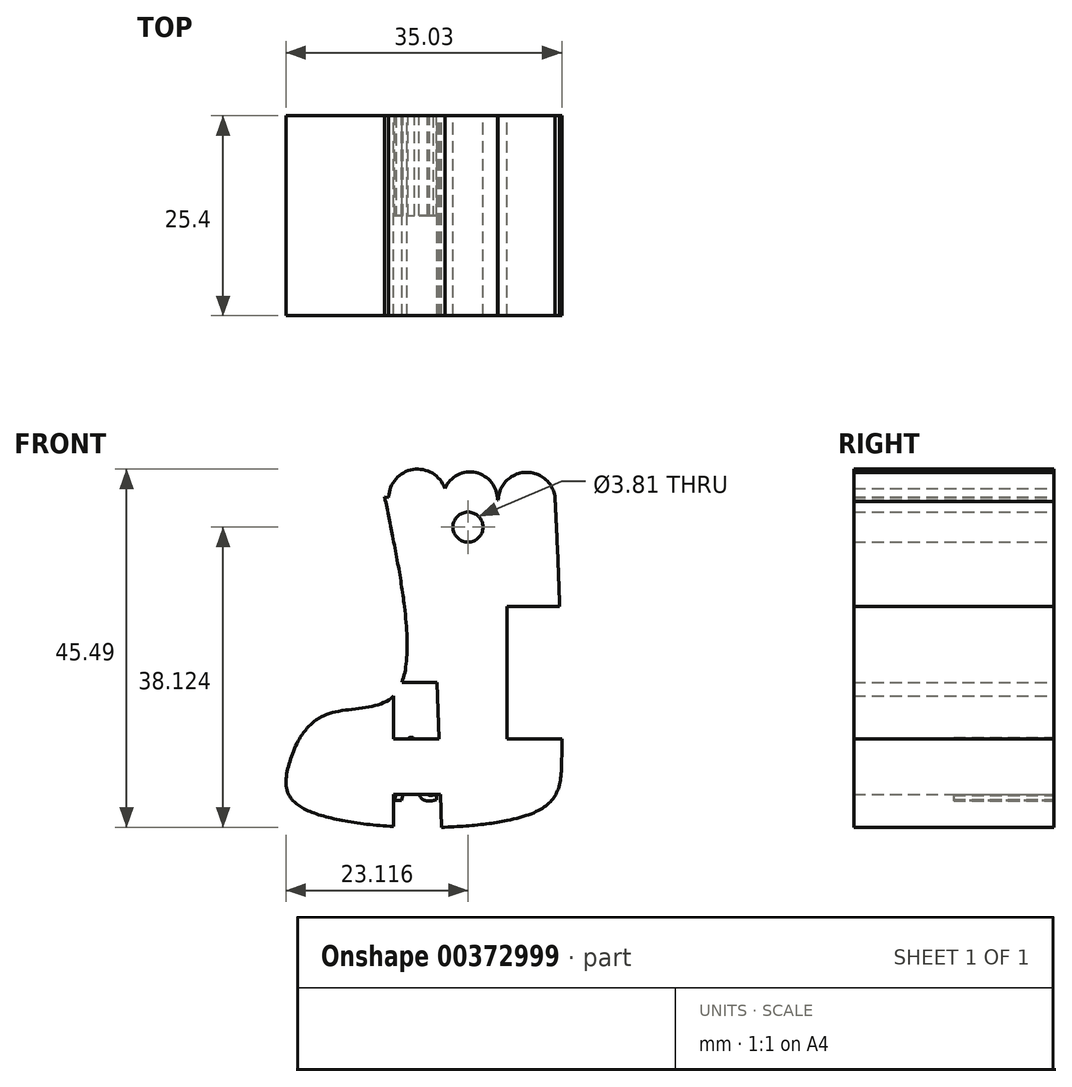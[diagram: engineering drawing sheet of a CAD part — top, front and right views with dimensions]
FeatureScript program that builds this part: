
annotation { "Feature Type Name" : "Feature", "Feature Type Description" : "" }
export const myFeature = defineFeature(function(context is Context, id is Id, definition is map)
    precondition{}
    {
        {
            var Q0;
            Q0=qCreatedBy(makeId("Front.planeOp"),FACE);
            var sketch = newSketch(context, id + "F0", { "sketchPlane" : qUnion([Q0])});
            skLineSegment(sketch, "E0", {"start": v(-9.1, 9.51) * mm, "end": v(-9.1, 12.05) * mm});
            skLineSegment(sketch, "E1", {"start": v(-34.55, 9.51) * mm, "end": v(-34.55, 12.05) * mm});
            skPoint(sketch, "E2.orphan", {"position": v(-34.55, 34.91) * mm});
            skPoint(sketch, "E3.orphan", {"position": v(-9.1, 34.91) * mm});
            skFitSpline(sketch, "E4", {"points": [v(16.98, 45.2) * mm, v(18.1, 19.94) * mm, v(9.2, 17.45) * mm, v(4.77, 11.06) * mm, v(6.43, 5.79) * mm, v(36.14, 5.23) * mm, v(39.47, 12.45) * mm, v(39.2, 31.33) * mm, v(38.64, 44.65) * mm], "startDerivative": vector(39.66, -192.65) * mm, "endDerivative": vector(-4.86, 99.16) * mm});
            skLineSegment(sketch, "E5", {"start": v(16.98, 45.2) * mm, "end": v(38.64, 44.65) * mm});
            skArc(sketch, "E6", {"start": v(24.55, 43.7) * mm, "mid": v(21.91, 48.69) * mm, "end": v(17.5, 45.2) * mm});
            skArc(sketch, "E7", {"start": v(31.29, 44.84) * mm, "mid": v(27.23, 48.36) * mm, "end": v(24.55, 43.7) * mm});
            skArc(sketch, "E8", {"start": v(38.64, 44.65) * mm, "mid": v(35.1, 48.37) * mm, "end": v(31.4, 44.84) * mm});
            skLineSegment(sketch, "E9", {"start": v(18.05, 39.93) * mm, "end": v(38.84, 40.56) * mm});
            skLineSegment(sketch, "E10", {"start": v(9.2, 17.45) * mm, "end": v(9.2, 4.69) * mm});
            skLineSegment(sketch, "E11", {"start": v(18.1, 19.94) * mm, "end": v(18.1, 3.37) * mm});
            skLineSegment(sketch, "E12", {"start": v(23.08, 40.08) * mm, "end": v(24.2, 3.28) * mm});
            skLineSegment(sketch, "E13", {"start": v(32.51, 40.36) * mm, "end": v(32.51, 4.13) * mm});
            skLineSegment(sketch, "E14", {"start": v(19.24, 31.33) * mm, "end": v(39.2, 31.33) * mm});
            skLineSegment(sketch, "E15", {"start": v(18.1, 21.68) * mm, "end": v(39.4, 21.68) * mm});
            skPoint(sketch, "E15.startSnap0", {"position": v(23.64, 21.68) * mm});
            skPoint(sketch, "E15.endSnap0", {"position": v(23.64, 21.68) * mm});
            skLineSegment(sketch, "E16", {"start": v(6.16, 14.53) * mm, "end": v(39.47, 14.53) * mm});
            skLineSegment(sketch, "E17", {"start": v(4.77, 7.46) * mm, "end": v(38.71, 7.46) * mm});
            skSolve(sketch);
        }
        {
            var Q0;
            {var subQ0=sQuery(id+"F0.wireOp",EDGE,"E14");var subQ1=sQuery(id+"F0.wireOp",EDGE,"E12");var subQ2=makeQuery(id+"F0.imprint","INTERSECT",VERTEX,{"derivedFrom":[subQ1,subQ0]});Q0=makeQuery(id+"F0.imprint","IMPRINT",FACE,{"disambiguationData":[TD([[makeQuery(id+"F0.imprint","IMPRINT",EDGE,{"disambiguationData":[TD([[subQ2,-1.0]])],"derivedFrom":subQ1}),1.0]])]});}
            var Q1;
            {var subQ0=sQuery(id+"F0.wireOp",EDGE,"E12");var subQ1=sQuery(id+"F0.wireOp",EDGE,"E9");var subQ2=makeQuery(id+"F0.imprint","INTERSECT",VERTEX,{"derivedFrom":[subQ1,subQ0]});Q1=makeQuery(id+"F0.imprint","IMPRINT",FACE,{"disambiguationData":[TD([[makeQuery(id+"F0.imprint","IMPRINT",EDGE,{"disambiguationData":[TD([[subQ2,-1.0]])],"derivedFrom":subQ1}),-1.0]])]});}
            var Q2;
            {var subQ1=sQuery(id+"F0.wireOp",EDGE,"E4");var subQ7=sQuery(id+"F0.wireOp",EDGE,"E5");var subQ9=makeQuery(id+"F0.imprint","INTERSECT",VERTEX,{"derivedFrom":[subQ1,subQ7]});Q2=makeQuery(id+"F0.imprint","IMPRINT",FACE,{"disambiguationData":[TD([[makeQuery(id+"F0.imprint","IMPRINT",EDGE,{"disambiguationData":[TD([[subQ9,-1.0]])],"derivedFrom":subQ1}),1.0]])]});}
            var Q3;
            {var subQ0=sQuery(id+"F0.wireOp",EDGE,"E14");var subQ1=sQuery(id+"F0.wireOp",EDGE,"E4");var subQ2=makeQuery(id+"F0.imprint","INTERSECT",VERTEX,{"disambiguationData":[OD(0.0)],"derivedFrom":[subQ1,subQ0]});Q3=makeQuery(id+"F0.imprint","IMPRINT",FACE,{"disambiguationData":[TD([[makeQuery(id+"F0.imprint","IMPRINT",EDGE,{"disambiguationData":[TD([[subQ2,-1.0]])],"derivedFrom":subQ1}),1.0]])]});}
            var Q4;
            {var subQ0=sQuery(id+"F0.wireOp",EDGE,"E14");var subQ1=sQuery(id+"F0.wireOp",EDGE,"E4");var subQ2=makeQuery(id+"F0.imprint","INTERSECT",VERTEX,{"disambiguationData":[OD(0.0)],"derivedFrom":[subQ1,subQ0]});Q4=makeQuery(id+"F0.imprint","IMPRINT",FACE,{"disambiguationData":[TD([[makeQuery(id+"F0.imprint","IMPRINT",EDGE,{"disambiguationData":[TD([[subQ2,1.0]])],"derivedFrom":subQ1}),1.0]])]});}
            var Q5;
            {var subQ0=sQuery(id+"F0.wireOp",EDGE,"E15");var subQ1=sQuery(id+"F0.wireOp",EDGE,"E4");var subQ2=makeQuery(id+"F0.imprint","INTERSECT",VERTEX,{"disambiguationData":[OD(0.0)],"derivedFrom":[subQ1,subQ0]});Q5=makeQuery(id+"F0.imprint","IMPRINT",FACE,{"disambiguationData":[TD([[makeQuery(id+"F0.imprint","IMPRINT",EDGE,{"disambiguationData":[TD([[subQ2,1.0]])],"derivedFrom":subQ1}),1.0]])]});}
            var Q6;
            {var subQ0=sQuery(id+"F0.wireOp",EDGE,"E16");var subQ1=sQuery(id+"F0.wireOp",EDGE,"E4");var subQ2=makeQuery(id+"F0.imprint","INTERSECT",VERTEX,{"disambiguationData":[OD(1.0)],"derivedFrom":[subQ1,subQ0]});Q6=makeQuery(id+"F0.imprint","IMPRINT",FACE,{"disambiguationData":[TD([[makeQuery(id+"F0.imprint","IMPRINT",EDGE,{"disambiguationData":[TD([[subQ2,1.0]])],"derivedFrom":subQ1}),1.0]])]});}
            var Q7;
            {var subQ0=sQuery(id+"F0.wireOp",EDGE,"E12");var subQ1=sQuery(id+"F0.wireOp",EDGE,"E4");var subQ2=makeQuery(id+"F0.imprint","INTERSECT",VERTEX,{"derivedFrom":[subQ1,subQ0]});Q7=makeQuery(id+"F0.imprint","IMPRINT",FACE,{"disambiguationData":[TD([[makeQuery(id+"F0.imprint","IMPRINT",EDGE,{"disambiguationData":[TD([[subQ2,-1.0]])],"derivedFrom":subQ1}),1.0]])]});}
            var Q8;
            {var subQ0=sQuery(id+"F0.wireOp",EDGE,"E13");var subQ1=sQuery(id+"F0.wireOp",EDGE,"E4");var subQ2=makeQuery(id+"F0.imprint","INTERSECT",VERTEX,{"derivedFrom":[subQ1,subQ0]});Q8=makeQuery(id+"F0.imprint","IMPRINT",FACE,{"disambiguationData":[TD([[makeQuery(id+"F0.imprint","IMPRINT",EDGE,{"disambiguationData":[TD([[subQ2,-1.0]])],"derivedFrom":subQ1}),1.0]])]});}
            var Q9;
            {var subQ0=sQuery(id+"F0.wireOp",EDGE,"E15");var subQ1=sQuery(id+"F0.wireOp",EDGE,"E12");var subQ2=makeQuery(id+"F0.imprint","INTERSECT",VERTEX,{"derivedFrom":[subQ1,subQ0]});Q9=makeQuery(id+"F0.imprint","IMPRINT",FACE,{"disambiguationData":[TD([[makeQuery(id+"F0.imprint","IMPRINT",EDGE,{"disambiguationData":[TD([[subQ2,-1.0]])],"derivedFrom":subQ1}),1.0]])]});}
            var Q10;
            {var subQ0=sQuery(id+"F0.wireOp",EDGE,"E16");var subQ1=sQuery(id+"F0.wireOp",EDGE,"E11");var subQ2=makeQuery(id+"F0.imprint","INTERSECT",VERTEX,{"derivedFrom":[subQ1,subQ0]});Q10=makeQuery(id+"F0.imprint","IMPRINT",FACE,{"disambiguationData":[TD([[makeQuery(id+"F0.imprint","IMPRINT",EDGE,{"disambiguationData":[TD([[subQ2,-1.0]])],"derivedFrom":subQ1}),1.0]])]});}
            var Q11;
            {var subQ0=sQuery(id+"F0.wireOp",EDGE,"E9");var subQ1=sQuery(id+"F0.wireOp",EDGE,"E4");var subQ2=makeQuery(id+"F0.imprint","INTERSECT",VERTEX,{"disambiguationData":[OD(0.0)],"derivedFrom":[subQ1,subQ0]});Q11=makeQuery(id+"F0.imprint","IMPRINT",FACE,{"disambiguationData":[TD([[makeQuery(id+"F0.imprint","IMPRINT",EDGE,{"disambiguationData":[TD([[subQ2,-1.0]])],"derivedFrom":subQ1}),1.0]])]});}
            var Q12;
            {var subQ0=sQuery(id+"F0.wireOp",EDGE,"E14");var subQ1=sQuery(id+"F0.wireOp",EDGE,"E4");var subQ2=makeQuery(id+"F0.imprint","INTERSECT",VERTEX,{"disambiguationData":[OD(1.0)],"derivedFrom":[subQ1,subQ0]});Q12=makeQuery(id+"F0.imprint","IMPRINT",FACE,{"disambiguationData":[TD([[makeQuery(id+"F0.imprint","IMPRINT",EDGE,{"disambiguationData":[TD([[subQ2,-1.0]])],"derivedFrom":subQ1}),1.0]])]});}
            var Q13;
            {var subQ0=sQuery(id+"F0.wireOp",EDGE,"E10");var subQ1=sQuery(id+"F0.wireOp",EDGE,"E4");var subQ2=makeQuery(id+"F0.imprint","INTERSECT",VERTEX,{"disambiguationData":[OD(0.0)],"derivedFrom":[subQ1,subQ0]});Q13=makeQuery(id+"F0.imprint","IMPRINT",FACE,{"disambiguationData":[TD([[makeQuery(id+"F0.imprint","IMPRINT",EDGE,{"disambiguationData":[TD([[subQ2,1.0]])],"derivedFrom":subQ1}),1.0]])]});}
            var Q14;
            {var subQ0=sQuery(id+"F0.wireOp",EDGE,"E10");var subQ1=sQuery(id+"F0.wireOp",EDGE,"E4");var subQ2=makeQuery(id+"F0.imprint","INTERSECT",VERTEX,{"disambiguationData":[OD(1.0)],"derivedFrom":[subQ1,subQ0]});Q14=makeQuery(id+"F0.imprint","IMPRINT",FACE,{"disambiguationData":[TD([[makeQuery(id+"F0.imprint","IMPRINT",EDGE,{"disambiguationData":[TD([[subQ2,-1.0]])],"derivedFrom":subQ1}),1.0]])]});}
            var Q15;
            {var subQ0=sQuery(id+"F0.wireOp",EDGE,"E16");var subQ1=sQuery(id+"F0.wireOp",EDGE,"E10");var subQ2=makeQuery(id+"F0.imprint","INTERSECT",VERTEX,{"derivedFrom":[subQ1,subQ0]});Q15=makeQuery(id+"F0.imprint","IMPRINT",FACE,{"disambiguationData":[TD([[makeQuery(id+"F0.imprint","IMPRINT",EDGE,{"disambiguationData":[TD([[subQ2,-1.0]])],"derivedFrom":subQ1}),1.0]])]});}
            var Q16;
            {var subQ0=sQuery(id+"F0.wireOp",EDGE,"E11");var subQ1=sQuery(id+"F0.wireOp",EDGE,"E4");var subQ2=makeQuery(id+"F0.imprint","INTERSECT",VERTEX,{"disambiguationData":[OD(1.0)],"derivedFrom":[subQ1,subQ0]});Q16=makeQuery(id+"F0.imprint","IMPRINT",FACE,{"disambiguationData":[TD([[makeQuery(id+"F0.imprint","IMPRINT",EDGE,{"disambiguationData":[TD([[subQ2,-1.0]])],"derivedFrom":subQ1}),1.0]])]});}
            var Q17;
            {var subQ1=sQuery(id+"F0.wireOp",EDGE,"E4");var subQ7=sQuery(id+"F0.wireOp",EDGE,"E11");var subQ8=makeQuery(id+"F0.imprint","INTERSECT",VERTEX,{"disambiguationData":[OD(0.0)],"derivedFrom":[subQ1,subQ7]});Q17=makeQuery(id+"F0.imprint","IMPRINT",FACE,{"disambiguationData":[TD([[makeQuery(id+"F0.imprint","IMPRINT",EDGE,{"disambiguationData":[TD([[subQ8,1.0]])],"derivedFrom":subQ1}),1.0]])]});}
            var Q18;
            {var subQ0=sQuery(id+"F0.wireOp",EDGE,"E16");var subQ1=sQuery(id+"F0.wireOp",EDGE,"E12");var subQ2=makeQuery(id+"F0.imprint","INTERSECT",VERTEX,{"derivedFrom":[subQ1,subQ0]});Q18=makeQuery(id+"F0.imprint","IMPRINT",FACE,{"disambiguationData":[TD([[makeQuery(id+"F0.imprint","IMPRINT",EDGE,{"disambiguationData":[TD([[subQ2,-1.0]])],"derivedFrom":subQ1}),1.0]])]});}
            var Q19;
            {var subQ0=sQuery(id+"F0.wireOp",EDGE,"E6");var subQ1=sQuery(id+"F0.wireOp",EDGE,"E5");var subQ2=makeQuery(id+"F0.imprint","INTERSECT",VERTEX,{"disambiguationData":[OD(0.0)],"derivedFrom":[subQ1,subQ0]});Q19=makeQuery(id+"F0.imprint","IMPRINT",FACE,{"disambiguationData":[TD([[makeQuery(id+"F0.imprint","IMPRINT",EDGE,{"disambiguationData":[TD([[subQ2,-1.0]])],"derivedFrom":subQ1}),1.0]])]});}
            var Q20;
            {var subQ0=sQuery(id+"F0.wireOp",EDGE,"E8");Q20=makeQuery(id+"F0.imprint","IMPRINT",FACE,{"disambiguationData":[TD([[makeQuery(id+"F0.imprint","IMPRINT",EDGE,{"derivedFrom":subQ0}),1.0]])]});}
            var Q21;
            {var subQ0=sQuery(id+"F0.wireOp",EDGE,"E7");var subQ1=sQuery(id+"F0.wireOp",EDGE,"E5");var subQ2=makeQuery(id+"F0.imprint","INTERSECT",VERTEX,{"disambiguationData":[OD(0.0)],"derivedFrom":[subQ1,subQ0]});Q21=makeQuery(id+"F0.imprint","IMPRINT",FACE,{"disambiguationData":[TD([[makeQuery(id+"F0.imprint","IMPRINT",EDGE,{"disambiguationData":[TD([[subQ2,1.0]])],"derivedFrom":subQ1}),1.0]])]});}
            var Q22;
            {var subQ0=sQuery(id+"F0.wireOp",EDGE,"E7");var subQ1=sQuery(id+"F0.wireOp",EDGE,"E5");var subQ2=makeQuery(id+"F0.imprint","INTERSECT",VERTEX,{"disambiguationData":[OD(1.0)],"derivedFrom":[subQ1,subQ0]});Q22=makeQuery(id+"F0.imprint","IMPRINT",FACE,{"disambiguationData":[TD([[makeQuery(id+"F0.imprint","IMPRINT",EDGE,{"disambiguationData":[TD([[subQ2,-1.0]])],"derivedFrom":subQ1}),-1.0]])]});}
            var Q23;
            {var subQ0=sQuery(id+"F0.wireOp",EDGE,"E7");var subQ1=sQuery(id+"F0.wireOp",EDGE,"E5");var subQ2=makeQuery(id+"F0.imprint","INTERSECT",VERTEX,{"disambiguationData":[OD(1.0)],"derivedFrom":[subQ1,subQ0]});Q23=makeQuery(id+"F0.imprint","IMPRINT",FACE,{"disambiguationData":[TD([[makeQuery(id+"F0.imprint","IMPRINT",EDGE,{"disambiguationData":[TD([[subQ2,-1.0]])],"derivedFrom":subQ1}),1.0]])]});}
            var Q24;
            {var subQ0=sQuery(id+"F0.wireOp",EDGE,"E16");var subQ1=sQuery(id+"F0.wireOp",EDGE,"E4");var subQ2=makeQuery(id+"F0.imprint","INTERSECT",VERTEX,{"disambiguationData":[OD(0.0)],"derivedFrom":[subQ1,subQ0]});Q24=makeQuery(id+"F0.imprint","IMPRINT",FACE,{"disambiguationData":[TD([[makeQuery(id+"F0.imprint","IMPRINT",EDGE,{"disambiguationData":[TD([[subQ2,-1.0]])],"derivedFrom":subQ1}),1.0]])]});}
            var Q25;
            {var subQ0=sQuery(id+"F0.wireOp",EDGE,"E10");var subQ1=sQuery(id+"F0.wireOp",EDGE,"E4");var subQ2=makeQuery(id+"F0.imprint","INTERSECT",VERTEX,{"disambiguationData":[OD(1.0)],"derivedFrom":[subQ1,subQ0]});Q25=makeQuery(id+"F0.imprint","IMPRINT",FACE,{"disambiguationData":[TD([[makeQuery(id+"F0.imprint","IMPRINT",EDGE,{"disambiguationData":[TD([[subQ2,1.0]])],"derivedFrom":subQ1}),1.0]])]});}
            var Q26;
            {var subQ0=sQuery(id+"F0.wireOp",EDGE,"E10");var subQ1=sQuery(id+"F0.wireOp",EDGE,"E4");var subQ2=makeQuery(id+"F0.imprint","INTERSECT",VERTEX,{"disambiguationData":[OD(0.0)],"derivedFrom":[subQ1,subQ0]});Q26=makeQuery(id+"F0.imprint","IMPRINT",FACE,{"disambiguationData":[TD([[makeQuery(id+"F0.imprint","IMPRINT",EDGE,{"disambiguationData":[TD([[subQ2,-1.0]])],"derivedFrom":subQ1}),1.0]])]});}
            extrude(context, id + "F1", {"entities" : qUnion([Q0, Q1, Q2, Q3, Q4, Q5, Q6, Q7, Q8, Q9, Q10, Q11, Q12, Q13, Q14, Q15, Q16, Q17, Q18, Q19, Q20, Q21, Q22, Q23, Q24, Q25, Q26]), "depth" : 25.4 * mm});
        }
        {
            var Q0;
            Q0=qCreatedBy(makeId("Front.planeOp"),FACE);
            var sketch = newSketch(context, id + "F2", { "sketchPlane" : qUnion([Q0])});
            skText(sketch, "E18", { "text": "Kaitlyn", "fontName": "OpenSans-Italic.ttf"});
            skPoint(sketch, "E19", {"position": v(27.56, 41.4) * mm});
            const initialGuessF2  = {"E18": [0.00518, 0.00727, 1, 0, 0.0084]};
            skSetInitialGuess(sketch, initialGuessF2);
            skSolve(sketch);
        }
        {
            var Q0;
            Q0=sQuery(id+"F2.wireOp",VERTEX,"E19");
            var Q1;
            Q1=makeQuery(id+"F1.opExtrude","SWEPT_BODY",BODY,{"disambiguationData":[OSD([sQuery(id+"F0.wireOp",EDGE,"E4"),sQuery(id+"F0.wireOp",EDGE,"E5"),sQuery(id+"F0.wireOp",EDGE,"E6"),sQuery(id+"F0.wireOp",EDGE,"E7"),sQuery(id+"F0.wireOp",EDGE,"E8")])]});
            hole(context, id + "F3", {"style" : HoleStyle.SIMPLE, "endStyle" : HoleEndStyle.THROUGH, "oppositeDirection" : true, "holeDiameter" : 3.8 * mm, "isTappedThrough" : true, "tappedDepth" : 12.7 * mm, "tapClearance" : 3, "locations" : qUnion([Q0]), "scope" : qUnion([Q1])});
        }
        {
            var Q0;
            Q0=qCreatedBy(makeId("Front.planeOp"),FACE);
            var sketch = newSketch(context, id + "F4", { "sketchPlane" : qUnion([Q0])});
            skText(sketch, "E20", { "text": "Kaitlyn", "fontName": "OpenSans-Italic.ttf"});
            const initialGuessF4  = {"E20": [0.00573, 0.00671, 1, 0, 0.00783]};
            skSetInitialGuess(sketch, initialGuessF4);
            skSolve(sketch);
        }
        {
            var Q0;
            Q0 = qSketchRegion(id + "F4", true);
            extrude(context, id + "F5", {"entities" : qUnion([Q0]), "operationType" : NewBodyOperationType.ADD, "depth" : 12.7 * mm});
        }
    });
